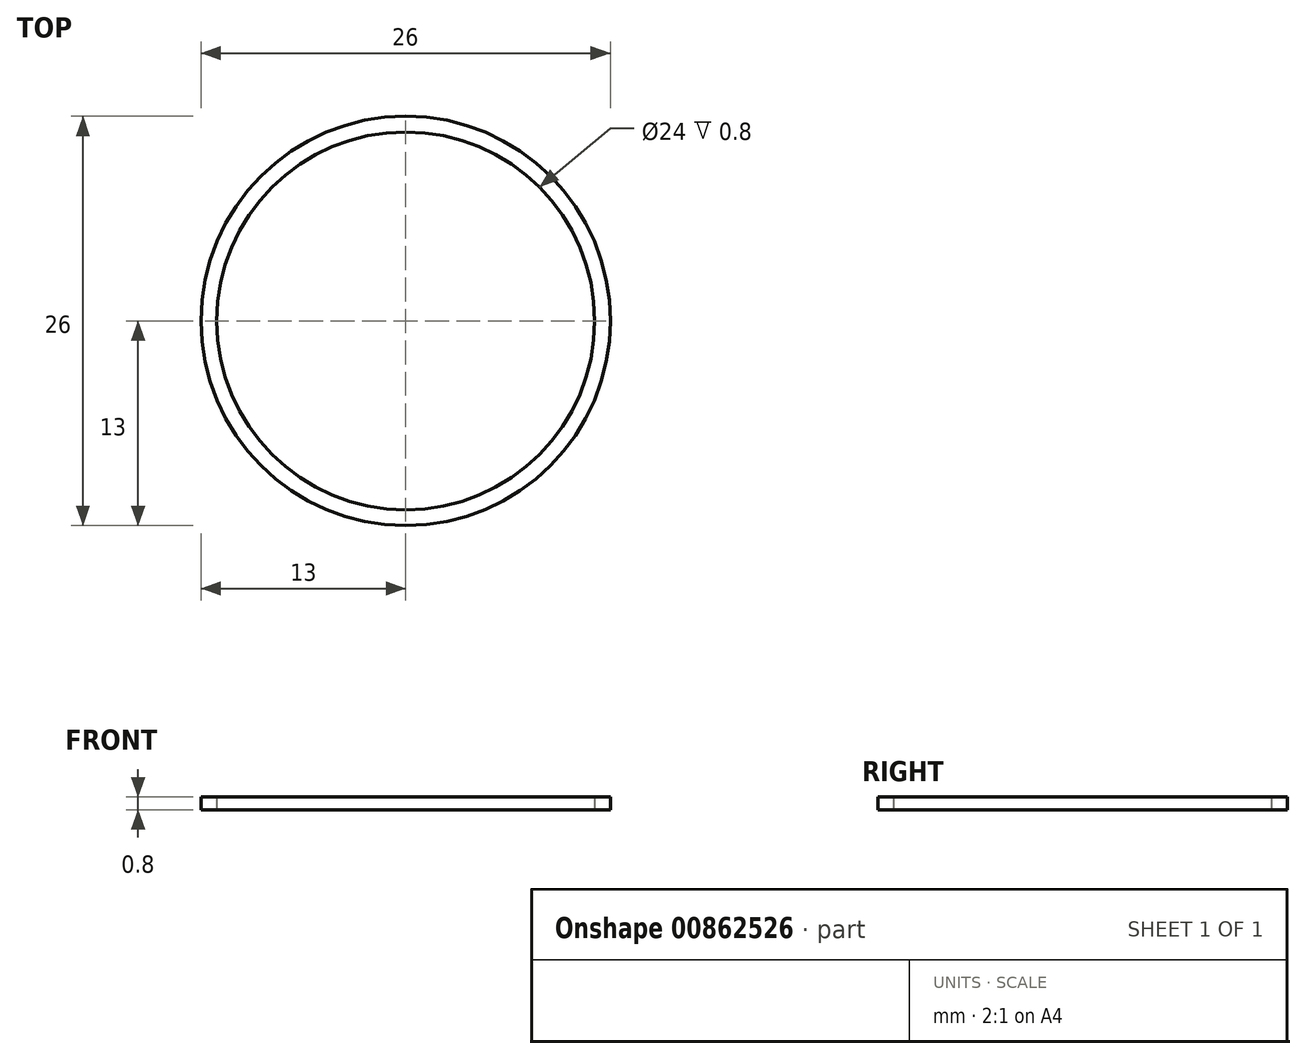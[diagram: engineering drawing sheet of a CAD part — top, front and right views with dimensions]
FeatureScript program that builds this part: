
annotation { "Feature Type Name" : "Feature", "Feature Type Description" : "" }
export const myFeature = defineFeature(function(context is Context, id is Id, definition is map)
    precondition{}
    {
        {
            var Q0;
            Q0=qCreatedBy(makeId("Top.planeOp"),FACE);
            var sketch = newSketch(context, id + "F0", { "sketchPlane" : qUnion([Q0])});
            skCircle(sketch, "E0", {"center": v(0, 0) * mm, "radius": 12 * mm});
            skCircle(sketch, "E1", {"center": v(0, 0) * mm, "radius": 13 * mm});
            skSolve(sketch);
        }
        {
            var Q0;
            Q0=makeQuery(id+"F0.imprint","IMPRINT",FACE,{"disambiguationData":[TD([[makeQuery(id+"F0.imprint","IMPRINT",EDGE,{"derivedFrom":sQuery(id+"F0.wireOp",EDGE,"E0")}),-1.0]])]});
            extrude(context, id + "F1", {"entities" : qUnion([Q0]), "depth" : 0.8 * mm, "offsetDistance" : 25 * mm});
        }
    });
